# Revit family: Framery Four
name_source: partatom
category: Furniture Systems
units: mm (PartAtom-declared; Revit-internal decimal feet)

## family parameters
Always vertical = Yes
Cut with Voids When Loaded = No
Part Type = Normal
Room Calculation Point = No
Round Connector Dimension = Use Diameter
Shared = No
Work Plane-Based = No

## types (2) — shared parameters
Assembly Code = 5111
Framery_table = Yes
Keynote = 8192
Manufacturer = Framery Oy
TD_Area_ = 2.64 m²
TD_BIM_content_publish_Revit_version_ = Revit 2021.1.9
TD_BIM_content_publish_date_ = 26.02.2024
TD_Collection_name_ = Framery Four
TD_Depth_ = 1200 mm
TD_Height_ = 2220 mm  [stored 7.28346 ft]
TD_Product_category_ = Meeting pods
TD_Weight_ = 630.00 kg
TD_Width_ = 2200 mm
zero-valued in all types: Default Elevation

## per-type parameters (varying)
| type | Framery_Coat_hooks_ | Framery_Cushion_ | Model | TD_Additional_information_ |
| Essentials | Yes | Yes | Four Essentials |  |
| Lite | No | No | Four Lite | Exterior optional colors - extra price
Interior panel optional colors - extra price
Carpet optional colors - extra price
Sofas with optional fabrics - extra price
Table with optional surface - extra price |

note: [stored X ft] marks values corroborated as IEEE doubles in the binary element streams (Revit-internal decimal feet)

## geometry (parser evidence)
native form markers: Sweep x40
no freeform markers — native parametric forms only
